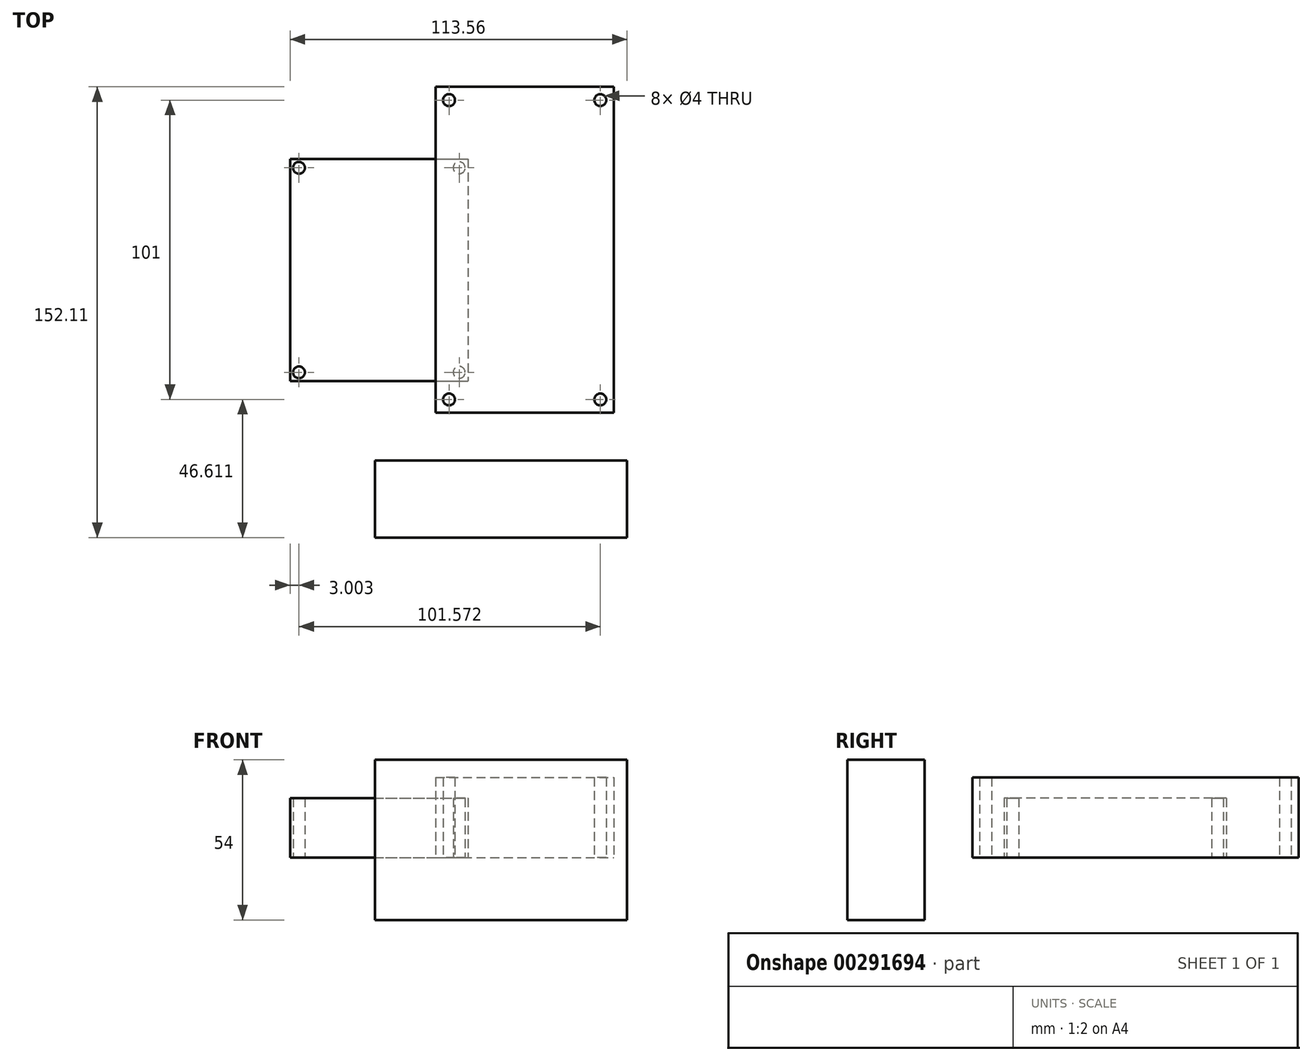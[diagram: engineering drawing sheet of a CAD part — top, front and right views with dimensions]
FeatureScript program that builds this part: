
annotation { "Feature Type Name" : "Feature", "Feature Type Description" : "" }
export const myFeature = defineFeature(function(context is Context, id is Id, definition is map)
    precondition{}
    {
        {
            var Q0;
            Q0=qCreatedBy(makeId("Front.planeOp"),FACE);
            var sketch = newSketch(context, id + "F0", { "sketchPlane" : qUnion([Q0])});
            skLineSegment(sketch, "E0.bottom", {"start": v(-47.58, 32.95) * mm, "end": v(37.42, 32.95) * mm});
            skLineSegment(sketch, "E0.top", {"start": v(-47.58, -21.05) * mm, "end": v(37.42, -21.05) * mm});
            skLineSegment(sketch, "E0.left", {"start": v(-47.58, 32.95) * mm, "end": v(-47.58, -21.05) * mm});
            skLineSegment(sketch, "E0.right", {"start": v(37.42, 32.95) * mm, "end": v(37.42, -21.05) * mm});
            skSolve(sketch);
        }
        {
            var Q0;
            Q0=makeQuery(id+"F0.imprint","IMPRINT",FACE,{"disambiguationData":[TD([[makeQuery(id+"F0.imprint","IMPRINT",EDGE,{"derivedFrom":sQuery(id+"F0.wireOp",EDGE,"E0.bottom")}),-1.0]])]});
            extrude(context, id + "F1", {"entities" : qUnion([Q0]), "depth" : 26 * mm, "offsetDistance" : 25 * mm});
        }
        {
            var Q0;
            Q0=qCreatedBy(makeId("Top.planeOp"),FACE);
            var sketch = newSketch(context, id + "F2", { "sketchPlane" : qUnion([Q0])});
            skLineSegment(sketch, "E1.bottom", {"start": v(-27.06, 126.11) * mm, "end": v(32.94, 126.11) * mm});
            skLineSegment(sketch, "E1.top", {"start": v(-27.06, 16.11) * mm, "end": v(32.94, 16.11) * mm});
            skLineSegment(sketch, "E1.left", {"start": v(-27.06, 126.11) * mm, "end": v(-27.06, 16.11) * mm});
            skLineSegment(sketch, "E1.right", {"start": v(32.94, 126.11) * mm, "end": v(32.94, 16.11) * mm});
            skCircle(sketch, "E2", {"center": v(-22.56, 121.61) * mm, "radius": 2 * mm});
            skCircle(sketch, "E3", {"center": v(28.44, 121.61) * mm, "radius": 2 * mm});
            skCircle(sketch, "E4", {"center": v(28.44, 20.61) * mm, "radius": 2 * mm});
            skCircle(sketch, "E5", {"center": v(-22.56, 20.61) * mm, "radius": 2 * mm});
            skSolve(sketch);
        }
        {
            var Q0;
            Q0=qCreatedBy(makeId("Top.planeOp"),FACE);
            var sketch = newSketch(context, id + "F3", { "sketchPlane" : qUnion([Q0])});
            skLineSegment(sketch, "E6.bottom", {"start": v(-76.14, 101.77) * mm, "end": v(-16.14, 101.77) * mm});
            skLineSegment(sketch, "E6.top", {"start": v(-76.14, 26.77) * mm, "end": v(-16.14, 26.77) * mm});
            skLineSegment(sketch, "E6.left", {"start": v(-76.14, 101.77) * mm, "end": v(-76.14, 26.77) * mm});
            skLineSegment(sketch, "E6.right", {"start": v(-16.14, 101.77) * mm, "end": v(-16.14, 26.77) * mm});
            skCircle(sketch, "E7", {"center": v(-73.14, 98.77) * mm, "radius": 2 * mm});
            skCircle(sketch, "E8", {"center": v(-19.14, 98.77) * mm, "radius": 2 * mm});
            skCircle(sketch, "E9", {"center": v(-19.14, 29.77) * mm, "radius": 2 * mm});
            skCircle(sketch, "E10", {"center": v(-73.14, 29.77) * mm, "radius": 2 * mm});
            skSolve(sketch);
        }
        {
            var Q0;
            Q0 = qSketchRegion(id + "F3", true);
            extrude(context, id + "F4", {"entities" : qUnion([Q0]), "depth" : 20 * mm, "offsetDistance" : 25 * mm});
        }
        {
            var Q0;
            Q0=makeQuery(id+"F2.imprint","IMPRINT",FACE,{"disambiguationData":[TD([[makeQuery(id+"F2.imprint","IMPRINT",EDGE,{"derivedFrom":sQuery(id+"F2.wireOp",EDGE,"E1.bottom")}),-1.0]])]});
            extrude(context, id + "F5", {"entities" : qUnion([Q0]), "depth" : 27 * mm, "offsetDistance" : 25 * mm});
        }
    });
